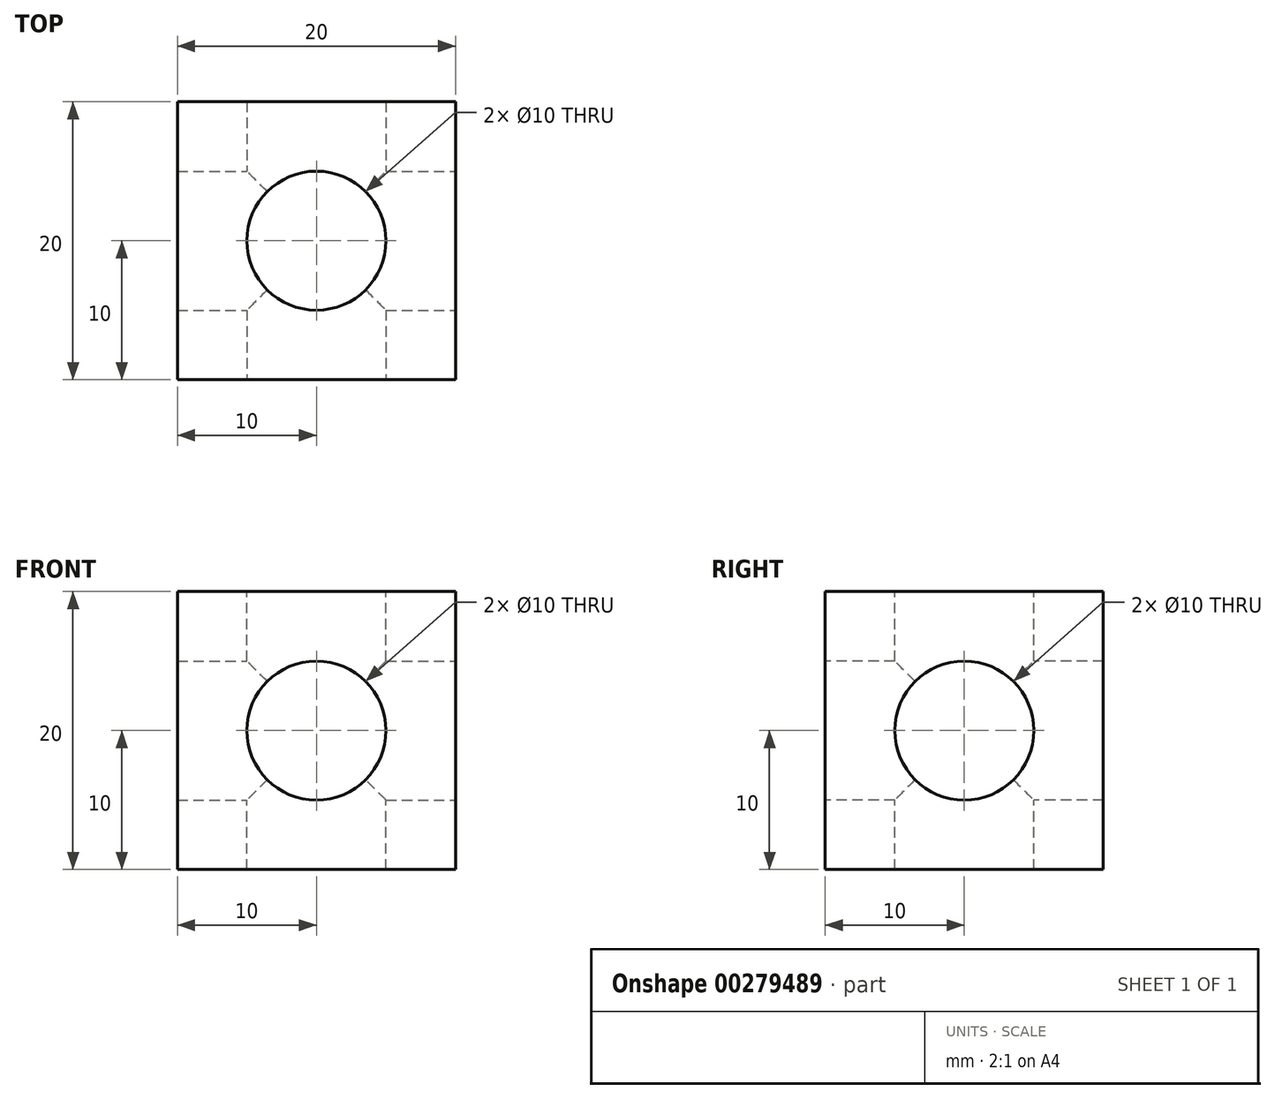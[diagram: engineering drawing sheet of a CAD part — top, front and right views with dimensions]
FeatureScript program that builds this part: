
annotation { "Feature Type Name" : "Feature", "Feature Type Description" : "" }
export const myFeature = defineFeature(function(context is Context, id is Id, definition is map)
    precondition{}
    {
        {
            var Q0;
            Q0=qCreatedBy(makeId("Top.planeOp"),FACE);
            var sketch = newSketch(context, id + "F0", { "sketchPlane" : qUnion([Q0])});
            skLineSegment(sketch, "E0.bottom", {"start": v(0, 0) * mm, "end": v(20, 0) * mm});
            skLineSegment(sketch, "E0.top", {"start": v(0, 20) * mm, "end": v(20, 20) * mm});
            skLineSegment(sketch, "E0.left", {"start": v(0, 0) * mm, "end": v(0, 20) * mm});
            skLineSegment(sketch, "E0.right", {"start": v(20, 0) * mm, "end": v(20, 20) * mm});
            skSolve(sketch);
        }
        {
            var Q0;
            Q0=makeQuery(id+"F0.imprint","IMPRINT",FACE,{"disambiguationData":[TD([[makeQuery(id+"F0.imprint","IMPRINT",EDGE,{"derivedFrom":sQuery(id+"F0.wireOp",EDGE,"E0.bottom")}),1.0]])]});
            extrude(context, id + "F1", {"entities" : qUnion([Q0]), "depth" : 20 * mm});
        }
        {
            var Q0;
            Q0=makeQuery(id+"F1.opExtrude","CAP_FACE",FACE,{"disambiguationData":[OSD([sQuery(id+"F0.wireOp",EDGE,"E0.bottom"),sQuery(id+"F0.wireOp",EDGE,"E0.top"),sQuery(id+"F0.wireOp",EDGE,"E0.left"),sQuery(id+"F0.wireOp",EDGE,"E0.right")])],"isStart":false});
            var sketch = newSketch(context, id + "F2", { "sketchPlane" : qUnion([Q0])});
            skCircle(sketch, "E1", {"center": v(10, 10) * mm, "radius": 5 * mm});
            skSolve(sketch);
        }
        {
            var Q0;
            Q0=makeQuery(id+"F2.imprint","IMPRINT",FACE,{"disambiguationData":[TD([[makeQuery(id+"F2.imprint","IMPRINT",EDGE,{"derivedFrom":sQuery(id+"F2.wireOp",EDGE,"E1")}),1.0]])]});
            extrude(context, id + "F3", {"entities" : qUnion([Q0]), "operationType" : NewBodyOperationType.REMOVE, "oppositeDirection" : true, "depth" : 25 * mm});
        }
        {
            var Q0;
            Q0=makeQuery(id+"F1.opExtrude","SWEPT_FACE",FACE,{"disambiguationData":[OSD([sQuery(id+"F0.wireOp",EDGE,"E0.bottom")])]});
            var sketch = newSketch(context, id + "F4", { "sketchPlane" : qUnion([Q0])});
            skCircle(sketch, "E2", {"center": v(10, 10) * mm, "radius": 5 * mm});
            skSolve(sketch);
        }
        {
            var Q0;
            Q0=makeQuery(id+"F4.imprint","IMPRINT",FACE,{"disambiguationData":[TD([[makeQuery(id+"F4.imprint","IMPRINT",EDGE,{"derivedFrom":sQuery(id+"F4.wireOp",EDGE,"E2")}),1.0]])]});
            extrude(context, id + "F5", {"entities" : qUnion([Q0]), "operationType" : NewBodyOperationType.REMOVE, "oppositeDirection" : true, "depth" : 25 * mm});
        }
        {
            var Q0;
            Q0=makeQuery(id+"F1.opExtrude","SWEPT_FACE",FACE,{"disambiguationData":[OSD([sQuery(id+"F0.wireOp",EDGE,"E0.right")])]});
            var sketch = newSketch(context, id + "F6", { "sketchPlane" : qUnion([Q0])});
            skCircle(sketch, "E3", {"center": v(10, 10) * mm, "radius": 5 * mm});
            skSolve(sketch);
        }
        {
            var Q0;
            Q0=makeQuery(id+"F6.imprint","IMPRINT",FACE,{"disambiguationData":[TD([[makeQuery(id+"F6.imprint","IMPRINT",EDGE,{"derivedFrom":sQuery(id+"F6.wireOp",EDGE,"E3")}),1.0]])]});
            extrude(context, id + "F7", {"entities" : qUnion([Q0]), "operationType" : NewBodyOperationType.REMOVE, "oppositeDirection" : true, "depth" : 25 * mm});
        }
    });
